# Revit family: E型变焦红外枪带视场
name_source: partatom
category: 常规模型
revit_build: Autodesk Revit 2016 (Build: 20150220_1215(x64)
units: mm (PartAtom-declared; Revit-internal decimal feet)

## family parameters
主体 = 面
共享 = 否
加载时剪切的空心 = 否
可将钢筋附着到主体 = 否
圆形连接件大小 = 使用直径
房间计算点 = 否
零件类型 = 标准

## types (2) — shared parameters
VR材质 = VR材质
默认高程 = 1219

## per-type parameters (varying)
| type | Day/Night | FOV Focal Length Maximum | FOV Focal Length Minimum | Image Sensor | Lens | Max.IR Distance | Minimum Illumination | Operating Temperature | Resolution | Weight | Wide Dynamic Range |
| HFW5830E-Z |  | 0  [stored 0 ft] | 0  [stored 0 ft] |  | 12  [stored 0.0393701 ft] |  |  |  |  | 0.00 kg |  |
| HFW8232E-Z | ICR | 16  [stored 0.0524934 ft] | 4  [stored 0.0131234 ft] | 1/1.9"2Mp Exmor CMOS | 4  [stored 0.0131234 ft] | 50m(164ft) | 0.02Lux/F1.53(Color) 0Lux/F1.53(IR on) | -40℃~+60℃(-40℉~+140℉) | 1920*1080 | 1.12 kg | 120dB |

note: [stored X ft] marks values corroborated as IEEE doubles in the binary element streams (Revit-internal decimal feet)
